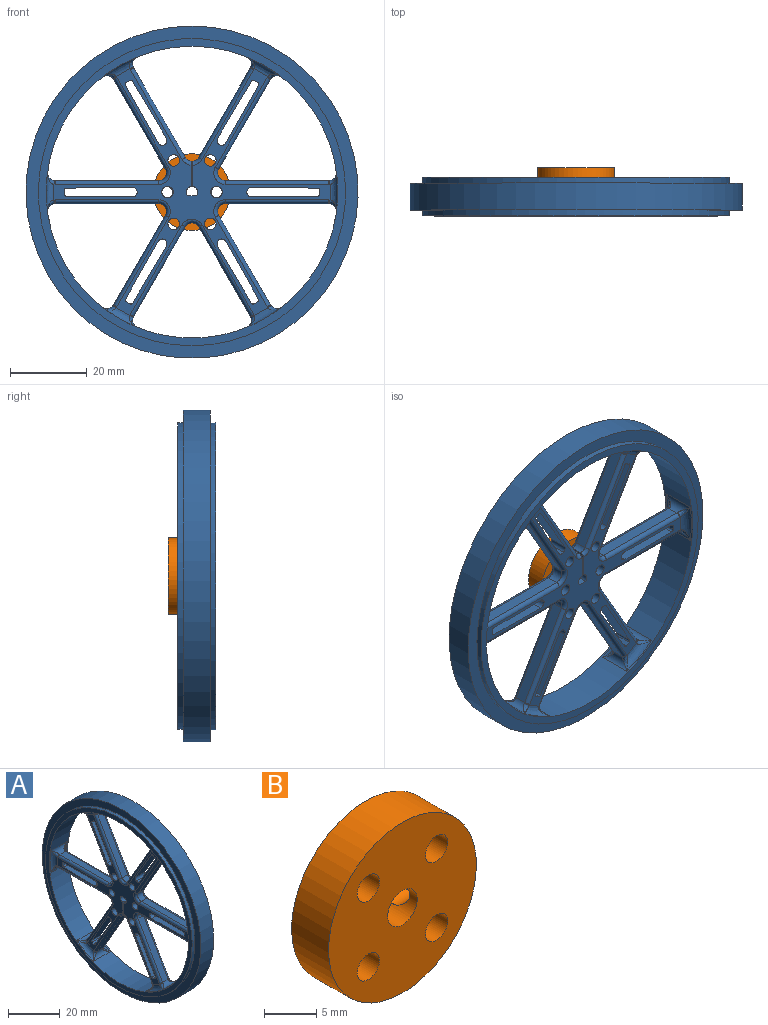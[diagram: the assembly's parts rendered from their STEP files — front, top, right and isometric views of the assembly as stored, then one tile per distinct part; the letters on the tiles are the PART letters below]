
ASSEMBLY  parts=2 mates=1
PART A: 192 faces, bbox 10x86.5x86.5 mm
  f0: plane 5x0.96mm, normal (0,-0.5,-0.87), area 5.6mm2, adj f6,f7,f152,f156
  f1: plane 5x0.96mm, normal (0,0.5,-0.87), area 5.6mm2, adj f8,f9,f152,f156
  f2: plane 5x1.11mm, normal (0,1,0), area 5.6mm2, adj f10,f11,f152,f156
  f3: plane 5x0.96mm, normal (0,0.5,0.87), area 5.6mm2, adj f12,f13,f152,f156
  f4: plane 5x0.96mm, normal (0,-0.5,0.87), area 5.6mm2, adj f14,f15,f152,f156
  f5: plane 5x1.11mm, normal (0,-1,0), area 5.6mm2, adj f16,f17,f152,f156
  f6: cylinder r=0.5mm len=5mm, axis (1,0,0), area 3.9mm2, adj f0,f66,f152,f156
  f7: cylinder r=0.5mm len=5mm, axis (1,0,0), area 3.9mm2, adj f0,f67,f152,f156
  f8: cylinder r=0.5mm len=5mm, axis (1,0,0), area 3.9mm2, adj f1,f70,f152,f156
  f9: cylinder r=0.5mm len=5mm, axis (1,0,0), area 3.9mm2, adj f1,f71,f152,f156
  f10: cylinder r=0.5mm len=5mm, axis (1,0,0), area 3.9mm2, adj f2,f74,f152,f156
  f11: cylinder r=0.5mm len=5mm, axis (1,0,0), area 3.9mm2, adj f2,f75,f152,f156
  f12: cylinder r=0.5mm len=5mm, axis (1,0,0), area 3.9mm2, adj f3,f78,f152,f156
  f13: cylinder r=0.5mm len=5mm, axis (1,0,0), area 3.9mm2, adj f3,f79,f152,f156
  f14: cylinder r=0.5mm len=5mm, axis (1,0,0), area 3.9mm2, adj f4,f82,f152,f156
  f15: cylinder r=0.5mm len=5mm, axis (1,0,0), area 3.9mm2, adj f4,f83,f152,f156
  f16: cylinder r=0.5mm len=5mm, axis (1,0,0), area 3.9mm2, adj f5,f87,f152,f156
  f17: cylinder r=0.5mm len=5mm, axis (1,0,0), area 3.9mm2, adj f5,f90,f152,f156
  f18: cylinder r=2mm len=3mm, axis (1,0,0), area 12.6mm2, adj f47,f115,f123,f124
  f19: revolved ~1.01x1mm, area 0.4mm2, adj f46,f125,f152,f163
  f20: revolved ~1.01x1mm, area 0.4mm2, adj f114,f126,f156,f163
  f21: revolved ~1.01x1mm, area 0.4mm2, adj f113,f127,f156,f165
  f22: revolved ~1.01x1mm, area 0.4mm2, adj f45,f128,f152,f165
  f23: cylinder r=2mm len=3mm, axis (1,0,0), area 12.6mm2, adj f44,f112,f129,f130
  f24: revolved ~1x0.97mm, area 0.4mm2, adj f43,f131,f152,f167
  f25: revolved ~1x0.97mm, area 0.4mm2, adj f111,f132,f156,f167
  f26: revolved ~1x1mm, area 0.4mm2, adj f110,f133,f156,f169
  f27: revolved ~1x1mm, area 0.4mm2, adj f59,f134,f152,f169
  f28: cylinder r=2mm len=3.46mm, axis (1,0,0), area 12.6mm2, adj f58,f109,f122,f135
  f29: revolved ~1x0.97mm, area 0.4mm2, adj f48,f136,f152,f161
  f30: cylinder r=2mm len=3mm, axis (1,0,0), area 5.5mm2, adj f50,f95,f96,f137
  f31: revolved ~1x1mm, area 0.4mm2, adj f49,f138,f152,f171
  f32: revolved ~1x0.97mm, area 0.4mm2, adj f116,f139,f156,f161
  f33: revolved ~1x1mm, area 0.4mm2, adj f94,f140,f156,f171
  f34: revolved ~1x1mm, area 0.4mm2, adj f108,f141,f156,f160
  f35: revolved ~1x0.97mm, area 0.4mm2, adj f107,f142,f156,f174
  f36: revolved ~1x1mm, area 0.4mm2, adj f57,f144,f152,f160
  f37: revolved ~1x0.97mm, area 0.4mm2, adj f56,f145,f152,f174
  f38: revolved ~1x0.97mm, area 0.4mm2, adj f53,f147,f152,f177
  f39: revolved ~1x0.97mm, area 0.4mm2, adj f103,f148,f156,f177
  f40: revolved ~1x1mm, area 0.4mm2, adj f102,f149,f156,f179
  f41: revolved ~1x1mm, area 0.4mm2, adj f52,f150,f152,f179
  f42: cylinder r=2mm len=3mm, axis (1,0,0), area 5.5mm2, adj f51,f100,f101,f151
  f43: cylinder r=1mm len=23.87mm, axis (0,-0.5,0.87), area 42.4mm2, adj f24,f44,f130,f152
  f44: revolved ~4.5x3mm, area 7.8mm2, adj f23,f43,f45,f152
  f45: cylinder r=1mm len=26.99mm, axis (0,1,0), area 42.4mm2, adj f22,f44,f129,f152
  f46: cylinder r=1mm len=26.99mm, axis (0,-1,0), area 42.4mm2, adj f19,f47,f124,f152
  f47: revolved ~4.5x3mm, area 7.8mm2, adj f18,f46,f48,f152
  f48: cylinder r=1mm len=23.87mm, axis (0,0.5,0.87), area 42.4mm2, adj f29,f47,f123,f152
  f49: cylinder r=1mm len=23.87mm, axis (0,-0.5,-0.87), area 42.4mm2, adj f31,f50,f137,f152
  f50: revolved ~2.43x1.99mm, area 3.5mm2, adj f30,f49,f96,f152
  f51: revolved ~2.43x1.99mm, area 3.5mm2, adj f42,f52,f100,f152
  f52: cylinder r=1mm len=23.87mm, axis (0,-0.5,0.87), area 42.4mm2, adj f41,f51,f151,f152
  f53: cylinder r=1mm len=23.87mm, axis (0,0.5,-0.87), area 42.4mm2, adj f38,f54,f146,f152
  f54: revolved ~4.5x3mm, area 7.8mm2, adj f53,f119,f120,f152
  f55: revolved ~4.5x3mm, area 7.8mm2, adj f56,f60,f61,f152
  f56: cylinder r=1mm len=23.87mm, axis (0,-0.5,-0.87), area 42.4mm2, adj f37,f55,f143,f152
  f57: cylinder r=1mm len=23.87mm, axis (0,0.5,0.87), area 42.4mm2, adj f36,f58,f122,f152
  f58: revolved ~5.2x2mm, area 7.8mm2, adj f28,f57,f59,f152
  f59: cylinder r=1mm len=23.87mm, axis (0,0.5,-0.87), area 42.4mm2, adj f27,f58,f135,f152
  f60: cylinder r=1mm len=26.99mm, axis (0,1,0), area 42.4mm2, adj f55,f62,f152,f153
  f61: cylinder r=2mm len=3mm, axis (1,0,0), area 12.6mm2, adj f55,f106,f143,f153
  f62: revolved ~1.01x1mm, area 0.4mm2, adj f60,f152,f154,f181
  f63: revolved ~1.01x1mm, area 0.4mm2, adj f105,f155,f156,f181
  f64: cylinder r=1.25mm len=5mm, axis (1,0,0), area 9.8mm2, adj f65,f67,f152,f156
  f65: cylinder r=1.25mm len=5mm, axis (1,0,0), area 9.8mm2, adj f64,f66,f152,f156
  f66: plane 14.84x8.78mm, normal (0,0.86,-0.51), area 86.2mm2, adj f6,f65,f152,f156
  f67: plane 15.02x8.46mm, normal (0,-0.87,0.49), area 86.2mm2, adj f7,f64,f152,f156
  f68: cylinder r=1.25mm len=5mm, axis (1,0,0), area 9.8mm2, adj f69,f71,f152,f156
  f69: cylinder r=1.25mm len=5mm, axis (1,0,0), area 9.8mm2, adj f68,f70,f152,f156
  f70: plane 15.02x8.46mm, normal (0,0.87,0.49), area 86.2mm2, adj f8,f69,f152,f156
  f71: plane 14.84x8.78mm, normal (0,-0.86,-0.51), area 86.2mm2, adj f9,f68,f152,f156
  f72: cylinder r=1.25mm len=5mm, axis (1,0,0), area 9.8mm2, adj f73,f75,f152,f156
  f73: cylinder r=1.25mm len=5mm, axis (1,0,0), area 9.8mm2, adj f72,f74,f152,f156
  f74: plane 17.24x5mm, normal (0,0.01,1), area 86.2mm2, adj f10,f73,f152,f156
  f75: plane 17.24x5mm, normal (0,0.01,-1), area 86.2mm2, adj f11,f72,f152,f156
  f76: cylinder r=1.25mm len=5mm, axis (1,0,0), area 9.8mm2, adj f77,f79,f152,f156
  f77: cylinder r=1.25mm len=5mm, axis (1,0,0), area 9.8mm2, adj f76,f78,f152,f156
  f78: plane 14.84x8.78mm, normal (0,-0.86,0.51), area 86.2mm2, adj f12,f77,f152,f156
  f79: plane 15.02x8.46mm, normal (0,0.87,-0.49), area 86.2mm2, adj f13,f76,f152,f156
  f80: cylinder r=1.25mm len=5mm, axis (1,0,0), area 9.8mm2, adj f81,f83,f152,f156
  f81: cylinder r=1.25mm len=5mm, axis (1,0,0), area 9.8mm2, adj f80,f82,f152,f156
  f82: plane 15.02x8.46mm, normal (0,-0.87,-0.49), area 86.2mm2, adj f14,f81,f152,f156
  f83: plane 14.84x8.78mm, normal (0,0.86,0.51), area 86.2mm2, adj f15,f80,f152,f156
  f84: cylinder r=1.5mm len=5mm, axis (1,0,0), area 47.1mm2, adj f152,f156
  f85: cylinder r=1.5mm len=5mm, axis (1,0,0), area 47.1mm2, adj f152,f156
  f86: cylinder r=1.5mm len=5mm, axis (1,0,0), area 47.1mm2, adj f152,f156
  f87: plane 17.24x5mm, normal (0,-0.01,1), area 86.2mm2, adj f16,f88,f152,f156
  f88: cylinder r=1.25mm len=5mm, axis (1,0,0), area 9.8mm2, adj f87,f89,f152,f156
  f89: cylinder r=1.25mm len=5mm, axis (1,0,0), area 9.8mm2, adj f88,f90,f152,f156
  f90: plane 17.24x5mm, normal (0,-0.01,-1), area 86.2mm2, adj f17,f89,f152,f156
  f91: cylinder r=1.5mm len=5mm, axis (1,0,0), area 47.1mm2, adj f152,f156
  f92: cylinder r=1.5mm len=5mm, axis (1,0,0), area 47.1mm2, adj f152,f156
  f93: cylinder r=1.5mm len=5mm, axis (1,0,0), area 47.1mm2, adj f152,f156
  f94: cylinder r=1mm len=23.87mm, axis (0,0.5,0.87), area 42.4mm2, adj f33,f95,f137,f156
  f95: revolved ~2.43x1.99mm, area 3.5mm2, adj f30,f94,f96,f156
  f96: plane 6.56x5.03mm, normal (0,1,0), area 32.3mm2, adj f30,f50,f95,f97,f152,f156
  f97: cylinder r=1.5mm len=5mm, axis (1,0,0), area 16mm2, adj f96,f98,f152,f156
  f98: plane 5x2.24mm, normal (0,0,-1), area 11.2mm2, adj f97,f99,f152,f156
  f99: cylinder r=1.5mm len=5mm, axis (1,0,0), area 16mm2, adj f98,f100,f152,f156
  f100: plane 6.56x5.03mm, normal (0,-1,0), area 32.3mm2, adj f42,f51,f99,f101,f152,f156
  f101: revolved ~2.43x1.99mm, area 3.5mm2, adj f42,f100,f102,f156
  f102: cylinder r=1mm len=23.87mm, axis (0,0.5,-0.87), area 42.4mm2, adj f40,f101,f151,f156
  f103: cylinder r=1mm len=23.87mm, axis (0,-0.5,0.87), area 42.4mm2, adj f39,f104,f146,f156
  f104: revolved ~4.5x3mm, area 7.8mm2, adj f103,f119,f121,f156
  f105: cylinder r=1mm len=26.99mm, axis (0,-1,0), area 42.4mm2, adj f63,f106,f153,f156
  f106: revolved ~4.5x3mm, area 7.8mm2, adj f61,f105,f107,f156
  f107: cylinder r=1mm len=23.87mm, axis (0,0.5,0.87), area 42.4mm2, adj f35,f106,f143,f156
  f108: cylinder r=1mm len=23.87mm, axis (0,-0.5,-0.87), area 42.4mm2, adj f34,f109,f122,f156
  f109: revolved ~5.2x2mm, area 7.8mm2, adj f28,f108,f110,f156
  f110: cylinder r=1mm len=23.87mm, axis (0,-0.5,0.87), area 42.4mm2, adj f26,f109,f135,f156
  f111: cylinder r=1mm len=23.87mm, axis (0,0.5,-0.87), area 42.4mm2, adj f25,f112,f130,f156
  f112: revolved ~4.5x3mm, area 7.8mm2, adj f23,f111,f113,f156
  f113: cylinder r=1mm len=26.99mm, axis (0,-1,0), area 42.4mm2, adj f21,f112,f129,f156
  f114: cylinder r=1mm len=26.99mm, axis (0,1,0), area 42.4mm2, adj f20,f115,f124,f156
  f115: revolved ~4.5x3mm, area 7.8mm2, adj f18,f114,f116,f156
  f116: cylinder r=1mm len=23.87mm, axis (0,-0.5,-0.87), area 42.4mm2, adj f32,f115,f123,f156
  f117: revolved ~1.01x1mm, area 0.4mm2, adj f121,f156,f157,f183
  f118: revolved ~1.01x1mm, area 0.4mm2, adj f120,f152,f158,f183
  f119: cylinder r=2mm len=3mm, axis (1,0,0), area 12.6mm2, adj f54,f104,f146,f159
  f120: cylinder r=1mm len=26.99mm, axis (0,-1,0), area 42.4mm2, adj f54,f118,f152,f159
  f121: cylinder r=1mm len=26.99mm, axis (0,1,0), area 42.4mm2, adj f104,f117,f156,f159
  f122: plane 23.37x13.5mm, normal (0,-0.87,0.5), area 81mm2, adj f28,f57,f108,f160
  f123: plane 23.37x13.5mm, normal (0,-0.87,0.5), area 81mm2, adj f18,f48,f116,f161
  f124: plane 26.99x3mm, normal (0,0,-1), area 81mm2, adj f18,f46,f114,f163
  f125: bspline ~3.26x3mm, area 2.3mm2, adj f19,f162,f163
  f126: bspline ~3.26x3mm, area 2.3mm2, adj f20,f163,f164
  f127: bspline ~3.26x3mm, area 2.3mm2, adj f21,f164,f165
  f128: bspline ~3.26x3mm, area 2.3mm2, adj f22,f162,f165
  f129: plane 26.99x3mm, normal (0,0,1), area 81mm2, adj f23,f45,f113,f165
  f130: plane 23.37x13.5mm, normal (0,-0.87,-0.5), area 81mm2, adj f23,f43,f111,f167
  f131: bspline ~3.67x3.01mm, area 2.3mm2, adj f24,f166,f167
  f132: bspline ~3.67x3mm, area 2.3mm2, adj f25,f167,f168
  f133: bspline ~3.09x3mm, area 2.3mm2, adj f26,f168,f169
  f134: bspline ~3.09x3mm, area 2.3mm2, adj f27,f166,f169
  f135: plane 23.37x13.5mm, normal (0,0.87,0.5), area 81mm2, adj f28,f59,f110,f169
  f136: bspline ~3.67x3mm, area 2.3mm2, adj f29,f161,f170
  f137: plane 23.37x13.5mm, normal (0,0.87,-0.5), area 81mm2, adj f30,f49,f94,f171
  f138: bspline ~3.09x3mm, area 2.3mm2, adj f31,f170,f171
  f139: bspline ~3.67x3mm, area 2.3mm2, adj f32,f161,f172
  f140: bspline ~3.09x3mm, area 2.3mm2, adj f33,f171,f172
  f141: bspline ~3.09x3mm, area 2.3mm2, adj f34,f160,f173
  f142: bspline ~3.67x3mm, area 2.3mm2, adj f35,f173,f174
  f143: plane 23.37x13.5mm, normal (0,0.87,-0.5), area 81mm2, adj f56,f61,f107,f174
  f144: bspline ~3.09x3.01mm, area 2.3mm2, adj f36,f160,f175
  f145: bspline ~3.67x3mm, area 2.3mm2, adj f37,f174,f175
  f146: plane 23.37x13.5mm, normal (0,0.87,0.5), area 81mm2, adj f53,f103,f119,f177
  f147: bspline ~3.67x3.01mm, area 2.3mm2, adj f38,f176,f177
  f148: bspline ~3.67x3mm, area 2.3mm2, adj f39,f177,f178
  f149: bspline ~3.09x3mm, area 2.3mm2, adj f40,f178,f179
  f150: bspline ~3.1x3mm, area 2.3mm2, adj f41,f176,f179
  f151: plane 23.37x13.5mm, normal (0,-0.87,-0.5), area 81mm2, adj f42,f52,f102,f179
  f152: plane 72.07x64.29mm, normal (1,0,0), area 550.1mm2, adj f0,f1,f2,f3,f4,f5,f6,f7
  f153: plane 26.99x3mm, normal (0,0,1), area 81mm2, adj f60,f61,f105,f181
  f154: bspline ~3.26x3mm, area 2.3mm2, adj f62,f180,f181
  f155: bspline ~3.26x3mm, area 2.3mm2, adj f63,f181,f182
  f156: plane 72.07x64.29mm, normal (-1,0,0), area 550.1mm2, adj f0,f1,f2,f3,f4,f5,f6,f7
  f157: bspline ~3.26x3mm, area 2.3mm2, adj f117,f182,f183
  f158: bspline ~3.26x3mm, area 2.3mm2, adj f118,f180,f183
  f159: plane 26.99x3mm, normal (0,0,-1), area 81mm2, adj f119,f120,f121,f183
  f160: cylinder r=2mm len=9mm, axis (1,0,0), area 17.4mm2, adj f34,f36,f122,f141,f144,f184
  f161: cylinder r=2mm len=9mm, axis (1,0,0), area 17.4mm2, adj f29,f32,f123,f136,f139,f184
  f162: revolved ~10.56x2.35mm, area 23mm2, adj f125,f128,f152,f184
  f163: cylinder r=2mm len=9mm, axis (1,0,0), area 17.4mm2, adj f19,f20,f124,f125,f126,f184
  f164: revolved ~10.56x2.35mm, area 23mm2, adj f126,f127,f156,f184
  f165: cylinder r=2mm len=9mm, axis (1,0,0), area 17.4mm2, adj f21,f22,f127,f128,f129,f184
  f166: revolved ~9.89x6.85mm, area 23mm2, adj f131,f134,f152,f184
  f167: cylinder r=2mm len=9mm, axis (1,0,0), area 17.4mm2, adj f24,f25,f130,f131,f132,f184
  f168: revolved ~9.89x6.85mm, area 23mm2, adj f132,f133,f156,f184
  f169: cylinder r=2mm len=9mm, axis (1,0,0), area 17.4mm2, adj f26,f27,f133,f134,f135,f184
  f170: revolved ~9.89x6.85mm, area 23mm2, adj f136,f138,f152,f184
  f171: cylinder r=2mm len=9mm, axis (1,0,0), area 17.4mm2, adj f31,f33,f137,f138,f140,f184
  f172: revolved ~9.89x6.85mm, area 23mm2, adj f139,f140,f156,f184
  f173: revolved ~9.89x6.85mm, area 23mm2, adj f141,f142,f156,f184
  f174: cylinder r=2mm len=9mm, axis (1,0,0), area 17.4mm2, adj f35,f37,f142,f143,f145,f184
  f175: revolved ~9.89x6.85mm, area 23mm2, adj f144,f145,f152,f184
  f176: revolved ~9.89x6.85mm, area 23mm2, adj f147,f150,f152,f184
  f177: cylinder r=2mm len=9mm, axis (1,0,0), area 17.4mm2, adj f38,f39,f146,f147,f148,f184
  f178: revolved ~9.89x6.85mm, area 23mm2, adj f148,f149,f156,f184
  f179: cylinder r=2mm len=9mm, axis (1,0,0), area 17.4mm2, adj f40,f41,f149,f150,f151,f184
  f180: revolved ~10.56x2.35mm, area 23mm2, adj f152,f154,f158,f184
  f181: cylinder r=2mm len=9mm, axis (1,0,0), area 17.4mm2, adj f62,f63,f153,f154,f155,f184
  f182: revolved ~10.56x2.35mm, area 23mm2, adj f155,f156,f157,f184
  f183: cylinder r=2mm len=9mm, axis (1,0,0), area 17.4mm2, adj f117,f118,f157,f158,f159,f184
  f184: cylinder r=38mm len=76mm, axis (1,0,0), area 1815.8mm2, adj f160,f161,f162,f163,f164,f165,f166,f167
  f185: plane 80x80mm, normal (-1,0,0), area 490.1mm2, adj f184,f187
  f186: plane 80x80mm, normal (1,0,0), area 490.1mm2, adj f184,f188
  f187: cylinder r=40mm len=80mm, axis (1,0,0), area 377mm2, adj f185,f189
  f188: cylinder r=40mm len=80mm, axis (-1,0,0), area 377mm2, adj f186,f190
  f189: plane 86.5x86.5mm, normal (-1,0,0), area 850mm2, adj f187,f191
  f190: plane 86.5x86.5mm, normal (1,0,0), area 850mm2, adj f188,f191
  f191: cylinder r=43.25mm len=86.5mm, axis (1,0,0), area 1902.2mm2, adj f189,f190
PART B: 9 faces, bbox 20x5x20 mm
  f0: cylinder r=1.5mm len=5mm, axis (0,-1,0), area 47.1mm2, adj f6,f7
  f1: cylinder r=1.5mm len=5mm, axis (0,-1,0), area 47.1mm2, adj f6,f7
  f2: cylinder r=2mm len=5mm, axis (0,-1,0), area 55.1mm2, adj f6,f7,f8
  f3: cylinder r=1.5mm len=5mm, axis (0,-1,0), area 47.1mm2, adj f6,f7
  f4: cylinder r=10mm len=20mm, axis (0,-1,0), area 307.1mm2, adj f6,f7,f8
  f5: cylinder r=1.5mm len=5mm, axis (0,-1,0), area 47.1mm2, adj f6,f7
  f6: plane 20x20mm, normal (0,1,0), area 273.3mm2, adj f0,f1,f2,f3,f4,f5
  f7: plane 20x20mm, normal (0,-1,0), area 273.3mm2, adj f0,f1,f2,f3,f4,f5
  f8: cylinder r=1.5mm len=8.68mm, axis (1,0,0), area 77.9mm2, adj f2,f4
PLACE A rot(axis=(-0.71,0.71,0),180deg) t=(35.23,51.43,72.15)mm
PLACE B rot(axis=(0,1,0),45deg) t=(35.23,53.93,72.15)mm
MATE revolute A.f97 <-> B.f2  axis (0,1,0) through (35.23,53.93,72.15)mm
